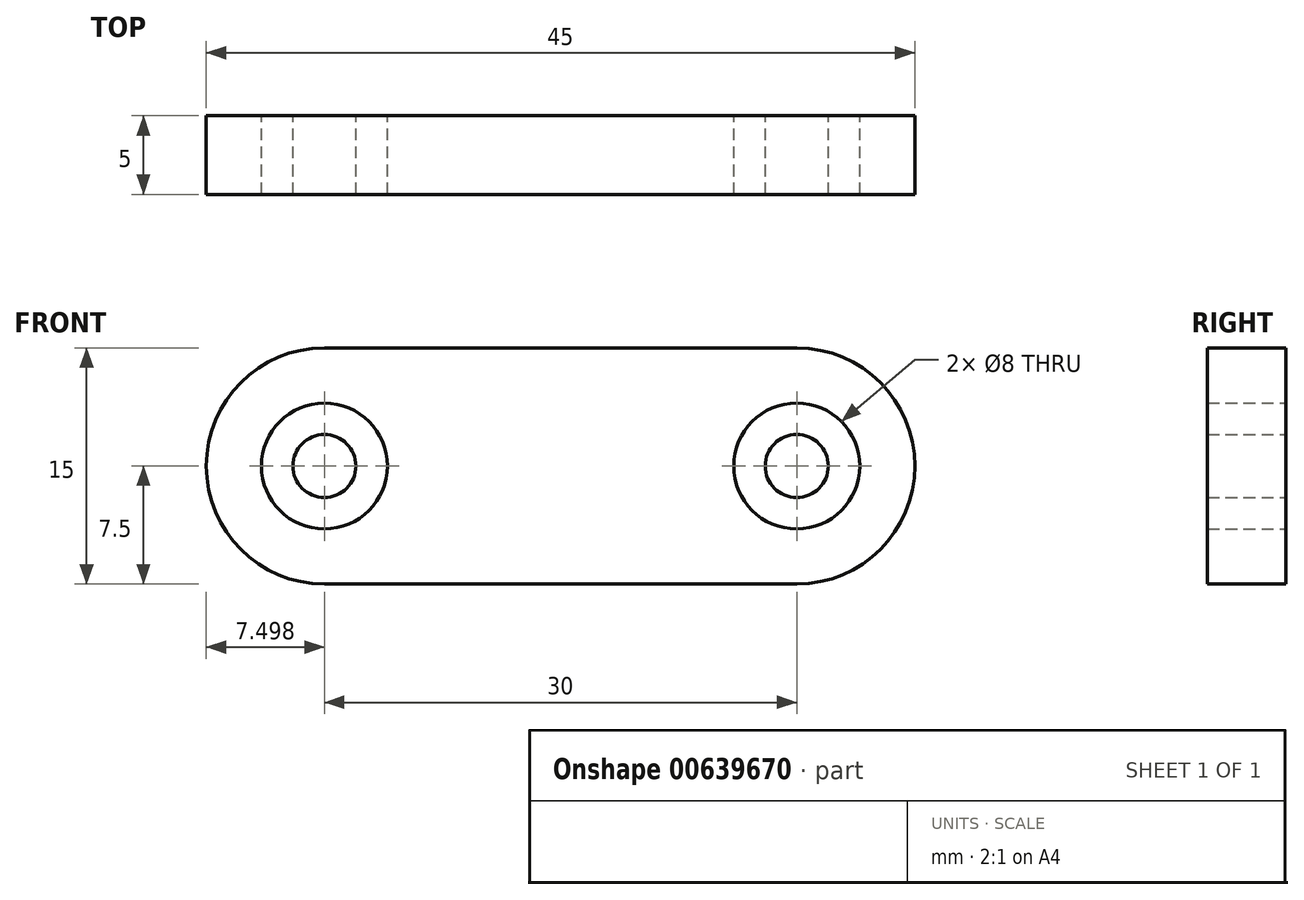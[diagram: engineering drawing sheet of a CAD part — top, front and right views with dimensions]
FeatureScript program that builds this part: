
annotation { "Feature Type Name" : "Feature", "Feature Type Description" : "" }
export const myFeature = defineFeature(function(context is Context, id is Id, definition is map)
    precondition{}
    {
        {
            var Q0;
            Q0=qCreatedBy(makeId("Front.planeOp"),FACE);
            var sketch = newSketch(context, id + "F0", { "sketchPlane" : qUnion([Q0])});
            skArc(sketch, "E0", {"start": v(-17.34, 7.5) * mm, "mid": v(-24.84, 0) * mm, "end": v(-17.34, -7.5) * mm});
            skArc(sketch, "E1", {"start": v(12.66, -7.5) * mm, "mid": v(20.16, 0) * mm, "end": v(12.66, 7.5) * mm});
            skLineSegment(sketch, "E2", {"start": v(-17.34, 7.5) * mm, "end": v(12.66, 7.5) * mm});
            skLineSegment(sketch, "E3", {"start": v(-17.34, -7.5) * mm, "end": v(12.66, -7.5) * mm});
            skCircle(sketch, "E4", {"center": v(-17.34, 0) * mm, "radius": 4 * mm});
            skCircle(sketch, "E5", {"center": v(12.66, 0) * mm, "radius": 4 * mm});
            skCircle(sketch, "E6", {"center": v(12.66, 0) * mm, "radius": 2 * mm});
            skCircle(sketch, "E7", {"center": v(-17.34, 0) * mm, "radius": 2 * mm});
            skSolve(sketch);
        }
        {
            var Q0;
            Q0=makeQuery(id+"F0.imprint","IMPRINT",FACE,{"disambiguationData":[TD([[makeQuery(id+"F0.imprint","IMPRINT",EDGE,{"derivedFrom":sQuery(id+"F0.wireOp",EDGE,"E0")}),1.0]])]});
            var Q1;
            Q1=makeQuery(id+"F0.imprint","IMPRINT",FACE,{"disambiguationData":[TD([[makeQuery(id+"F0.imprint","IMPRINT",EDGE,{"derivedFrom":sQuery(id+"F0.wireOp",EDGE,"E6")}),1.0]])]});
            var Q2;
            Q2=makeQuery(id+"F0.imprint","IMPRINT",FACE,{"disambiguationData":[TD([[makeQuery(id+"F0.imprint","IMPRINT",EDGE,{"derivedFrom":sQuery(id+"F0.wireOp",EDGE,"E7")}),1.0]])]});
            extrude(context, id + "F1", {"entities" : qUnion([Q0, Q1, Q2]), "depth" : 5 * mm, "offsetDistance" : 25.4 * mm});
        }
    });
